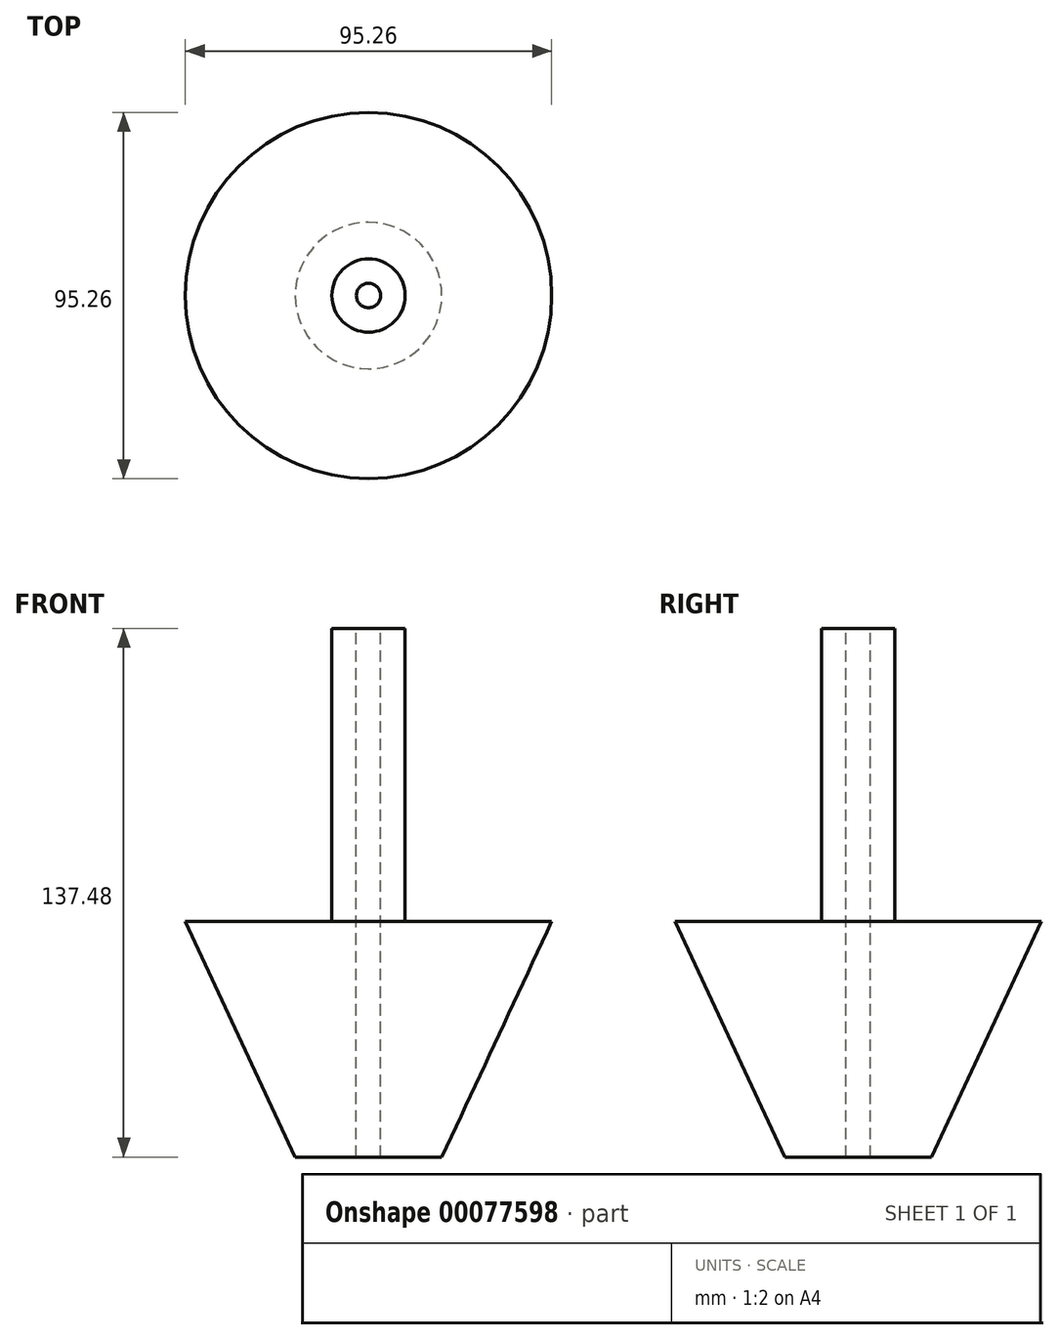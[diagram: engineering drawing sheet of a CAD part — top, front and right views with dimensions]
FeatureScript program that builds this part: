
annotation { "Feature Type Name" : "Feature", "Feature Type Description" : "" }
export const myFeature = defineFeature(function(context is Context, id is Id, definition is map)
    precondition{}
    {
        {
            var Q0;
            Q0=qCreatedBy(makeId("Front.planeOp"),FACE);
            var sketch = newSketch(context, id + "F0", { "sketchPlane" : qUnion([Q0])});
            skLineSegment(sketch, "E0", {"start": v(0, -61.28) * mm, "end": v(-19.05, -61.28) * mm});
            skLineSegment(sketch, "E1", {"start": v(-19.05, -61.28) * mm, "end": v(-47.63, 0) * mm});
            skLineSegment(sketch, "E2", {"start": v(-47.62, 0) * mm, "end": v(-9.53, 0) * mm});
            skLineSegment(sketch, "E3", {"start": v(-9.53, 0) * mm, "end": v(-9.53, 76.2) * mm});
            skLineSegment(sketch, "E4", {"start": v(-9.52, 76.2) * mm, "end": v(0, 76.2) * mm});
            skLineSegment(sketch, "E5", {"start": v(0, 76.2) * mm, "end": v(0, -61.28) * mm});
            skSolve(sketch);
        }
        {
            var Q0;
            Q0 = qSketchRegion(id + "F0", true);
            var Q1;
            Q1=sQuery(id+"F0.wireOp",EDGE,"E5");
            revolve(context, id + "F1", {"entities" : qUnion([Q0]), "axis" : qUnion([Q1]), "revolveType" : RevolveType.FULL});
        }
        {
            var Q0;
            Q0=makeQuery(id+"F1.opRevolve","SWEPT_FACE",FACE,{"disambiguationData":[OSD([sQuery(id+"F0.wireOp",EDGE,"E4")])]});
            var sketch = newSketch(context, id + "F2", { "sketchPlane" : qUnion([Q0])});
            skCircle(sketch, "E6", {"center": v(0, 0) * mm, "radius": 3.18 * mm});
            skSolve(sketch);
        }
        {
            var Q0;
            Q0 = qSketchRegion(id + "F2", true);
            extrude(context, id + "F3", {"entities" : qUnion([Q0]), "operationType" : NewBodyOperationType.REMOVE, "endBound" : BoundingType.THROUGH_ALL, "oppositeDirection" : true, "depth" : 25.4 * mm});
        }
    });
